# Revit family: HORIZONTAL_LOUVER_BLADE_SINGLE_SWING_GATE
name_source: partatom
category: Specialty Equipment
units: mm (PartAtom-declared; Revit-internal decimal feet)

## family parameters
Always vertical = No
Classification Number = 23.55.00.00
Cut with Voids When Loaded = No
Enable Cutting in Views = No
Maintain Annotation Orientation = No
Part Type = Normal
Room Calculation Point = No
Round Connector Dimension = Use Diameter
Shared = No
Work Plane-Based = No

## types (1)
- Assembly
    Assembly Code = F1020100
    Closed = Yes
    Default Elevation = 0' - 0"
    Description = Maximus Swing - Atlas
    Door Opening = 0.00°
    Drop Rod Visibility = No
    Handle Height = 2' - 11 7/16"
    Instruction Sheet Link = http://palmshieldlouvers.com
    Keynote = 05 10 00
    Louver Finish = Metal - PalmSHIELD - Traffic Black
    Manufacturer = PalmSHIELD
    Material = Metal - PalmSHIELD - Grey Beige
    Model = Maximus Swing - Atlas - Assembly
    Offset From Ground = 0' - 2"
    Open = No
    Product Documentation Link = http://palmshieldlouvers.com
    Product Page URL = https://palmshieldlouvers.com
    URL = https://palmshieldlouvers.com
    Version = 2020 - v1.0a
    Warranty URL = https://palmshieldlouvers.com

## geometry (parser evidence)
native form markers: Sweep x37
no freeform markers — native parametric forms only
